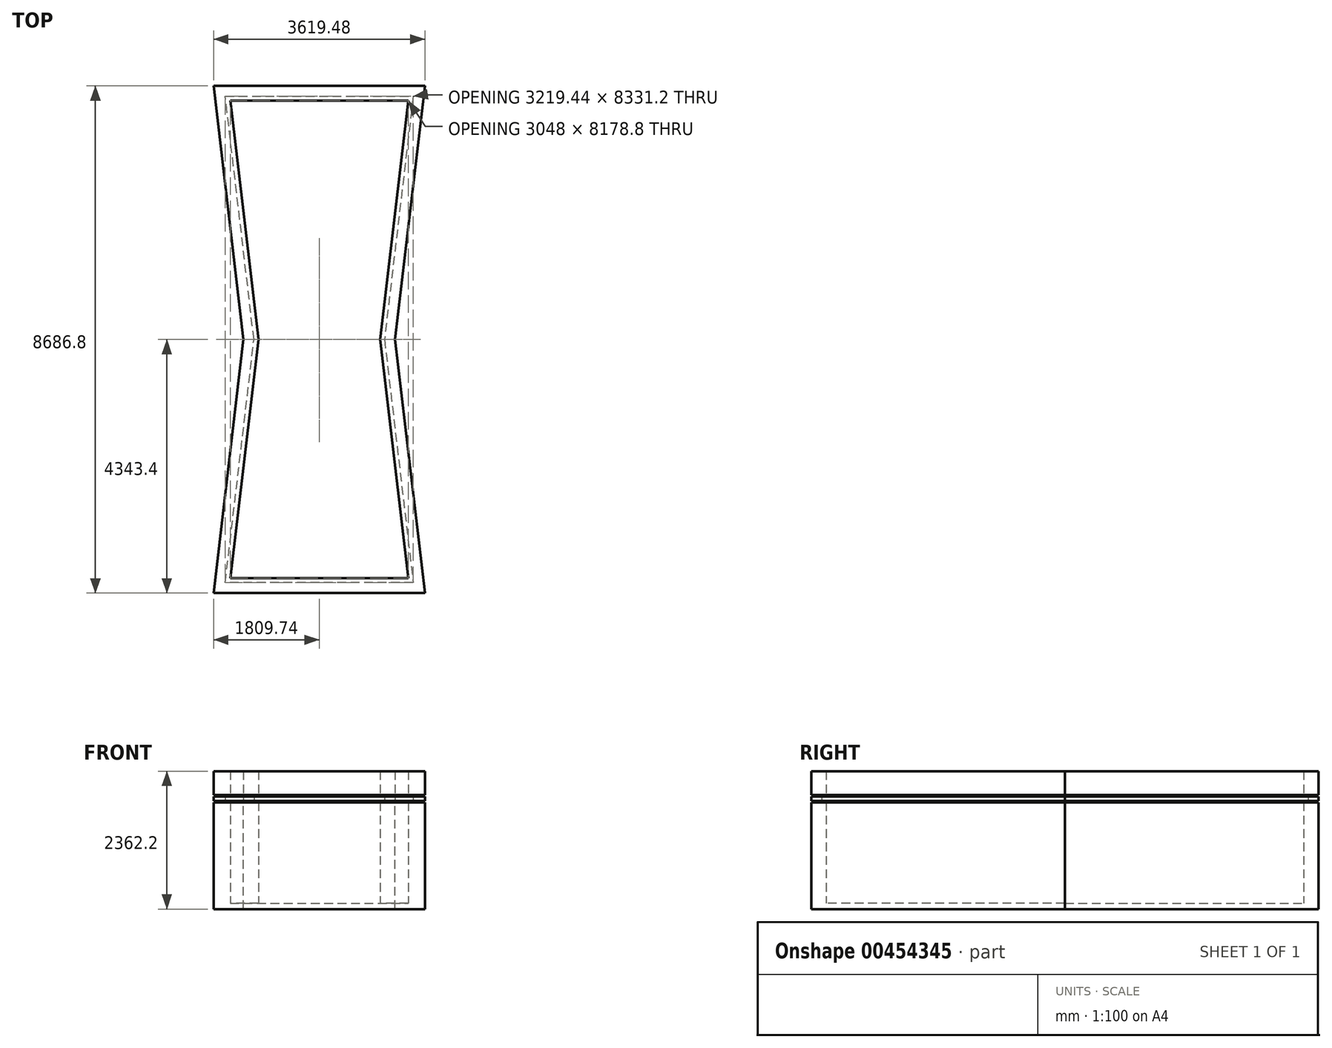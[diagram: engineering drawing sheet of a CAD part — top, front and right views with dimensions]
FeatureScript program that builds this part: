
annotation { "Feature Type Name" : "Feature", "Feature Type Description" : "" }
export const myFeature = defineFeature(function(context is Context, id is Id, definition is map)
    precondition{}
    {
        {
            var Q0;
            Q0=qCreatedBy(makeId("Top.planeOp"),FACE);
            var sketch = newSketch(context, id + "F0", { "sketchPlane" : qUnion([Q0])});
            skLineSegment(sketch, "E0", {"start": v(-1809.74, -4343.4) * mm, "end": v(-1297.16, 0) * mm});
            skLineSegment(sketch, "E1", {"start": v(-1297.16, 0) * mm, "end": v(-1809.74, 4343.4) * mm});
            skLineSegment(sketch, "E2", {"start": v(-1809.74, 4343.4) * mm, "end": v(1809.74, 4343.4) * mm});
            skLineSegment(sketch, "E3", {"start": v(1809.74, 4343.4) * mm, "end": v(1297.16, 0) * mm});
            skLineSegment(sketch, "E4", {"start": v(1297.16, 0) * mm, "end": v(1809.74, -4343.4) * mm});
            skLineSegment(sketch, "E5", {"start": v(1809.74, -4343.4) * mm, "end": v(-1809.74, -4343.4) * mm});
            skLineSegment(sketch, "E6", {"start": v(-1524, 4089.4) * mm, "end": v(1524, 4089.4) * mm});
            skLineSegment(sketch, "E7", {"start": v(1524, 4089.4) * mm, "end": v(1041.4, 0) * mm});
            skLineSegment(sketch, "E8", {"start": v(1041.4, 0) * mm, "end": v(1524, -4089.4) * mm});
            skLineSegment(sketch, "E9", {"start": v(1524, -4089.4) * mm, "end": v(-1524, -4089.4) * mm});
            skLineSegment(sketch, "E10", {"start": v(-1524, -4089.4) * mm, "end": v(-1041.4, 0) * mm});
            skLineSegment(sketch, "E11", {"start": v(-1041.4, 0) * mm, "end": v(-1524, 4089.4) * mm});
            skSolve(sketch);
        }
        {
            var Q0;
            Q0=makeQuery(id+"F0.imprint","IMPRINT",FACE,{"disambiguationData":[TD([[makeQuery(id+"F0.imprint","IMPRINT",EDGE,{"derivedFrom":sQuery(id+"F0.wireOp",EDGE,"E6")}),-1.0]])]});
            var Q1;
            Q1=makeQuery(id+"F0.imprint","IMPRINT",FACE,{"disambiguationData":[TD([[makeQuery(id+"F0.imprint","IMPRINT",EDGE,{"derivedFrom":sQuery(id+"F0.wireOp",EDGE,"E0")}),-1.0]])]});
            extrude(context, id + "F1", {"entities" : qUnion([Q0, Q1]), "oppositeDirection" : true, "depth" : 101.6 * mm});
        }
        {
            var Q0;
            Q0 = qSketchRegion(id + "F0", true);
            extrude(context, id + "F2", {"entities" : qUnion([Q0]), "operationType" : NewBodyOperationType.ADD, "depth" : 1727.2 * mm});
        }
        {
            var Q0;
            Q0=makeQuery(id+"F2.opExtrude","CAP_FACE",FACE,{"disambiguationData":[OSD([sQuery(id+"F0.wireOp",EDGE,"E0"),sQuery(id+"F0.wireOp",EDGE,"E1"),sQuery(id+"F0.wireOp",EDGE,"E2"),sQuery(id+"F0.wireOp",EDGE,"E3"),sQuery(id+"F0.wireOp",EDGE,"E4"),sQuery(id+"F0.wireOp",EDGE,"E5"),sQuery(id+"F0.wireOp",EDGE,"E6"),sQuery(id+"F0.wireOp",EDGE,"E7"),sQuery(id+"F0.wireOp",EDGE,"E8"),sQuery(id+"F0.wireOp",EDGE,"E9"),sQuery(id+"F0.wireOp",EDGE,"E10"),sQuery(id+"F0.wireOp",EDGE,"E11")])],"isStart":false});
            cPlane(context, id + "F3", {"entities" : qUnion([Q0]), "cplaneType" : CPlaneType.OFFSET, "offset" : 25.4 * mm, "width" : 152.4 * mm, "height" : 152.4 * mm});
        }
        {
            var Q0;
            Q0=qCreatedBy(id+"F3.planeOp",FACE);
            var sketch = newSketch(context, id + "F4", { "sketchPlane" : qUnion([Q0])});
            skLineSegment(sketch, "E12", {"start": v(-1809.74, -4343.4) * mm, "end": v(-1297.16, 0) * mm});
            skLineSegment(sketch, "E13", {"start": v(-1297.16, 0) * mm, "end": v(-1809.74, 4343.4) * mm});
            skLineSegment(sketch, "E14", {"start": v(-1809.74, 4343.4) * mm, "end": v(1809.74, 4343.4) * mm});
            skLineSegment(sketch, "E15", {"start": v(1809.74, 4343.4) * mm, "end": v(1297.16, 0) * mm});
            skLineSegment(sketch, "E16", {"start": v(1297.16, 0) * mm, "end": v(1809.74, -4343.4) * mm});
            skLineSegment(sketch, "E17", {"start": v(1809.74, -4343.4) * mm, "end": v(-1809.74, -4343.4) * mm});
            skLineSegment(sketch, "E18", {"start": v(-1609.72, -4165.6) * mm, "end": v(-1118.13, 0) * mm});
            skLineSegment(sketch, "E19", {"start": v(-1118.13, 0) * mm, "end": v(-1609.72, 4165.6) * mm});
            skLineSegment(sketch, "E20", {"start": v(-1609.72, 4165.6) * mm, "end": v(1609.72, 4165.6) * mm});
            skLineSegment(sketch, "E21", {"start": v(1609.72, 4165.6) * mm, "end": v(1118.13, 0) * mm});
            skLineSegment(sketch, "E22", {"start": v(1118.13, 0) * mm, "end": v(1609.72, -4165.6) * mm});
            skLineSegment(sketch, "E23", {"start": v(1609.72, -4165.6) * mm, "end": v(-1609.72, -4165.6) * mm});
            skLineSegment(sketch, "E24", {"start": v(-1524, 4089.4) * mm, "end": v(1524, 4089.4) * mm});
            skLineSegment(sketch, "E25", {"start": v(1524, 4089.4) * mm, "end": v(1041.4, 0) * mm});
            skLineSegment(sketch, "E26", {"start": v(1041.4, 0) * mm, "end": v(1524, -4089.4) * mm});
            skLineSegment(sketch, "E27", {"start": v(1524, -4089.4) * mm, "end": v(-1524, -4089.4) * mm});
            skLineSegment(sketch, "E28", {"start": v(-1524, -4089.4) * mm, "end": v(-1041.4, 0) * mm});
            skLineSegment(sketch, "E29", {"start": v(-1041.4, 0) * mm, "end": v(-1524, 4089.4) * mm});
            skSolve(sketch);
        }
        {
            var Q0;
            Q0 = qSketchRegion(id + "F4", true);
            extrude(context, id + "F5", {"entities" : qUnion([Q0]), "depth" : 76.2 * mm});
        }
        {
            var Q0;
            Q0=makeQuery(id+"F5.opExtrude","CAP_FACE",FACE,{"disambiguationData":[OSD([sQuery(id+"F4.wireOp",EDGE,"E12"),sQuery(id+"F4.wireOp",EDGE,"E13"),sQuery(id+"F4.wireOp",EDGE,"E14"),sQuery(id+"F4.wireOp",EDGE,"E15"),sQuery(id+"F4.wireOp",EDGE,"E16"),sQuery(id+"F4.wireOp",EDGE,"E17"),sQuery(id+"F4.wireOp",EDGE,"E18"),sQuery(id+"F4.wireOp",EDGE,"E19"),sQuery(id+"F4.wireOp",EDGE,"E20"),sQuery(id+"F4.wireOp",EDGE,"E21"),sQuery(id+"F4.wireOp",EDGE,"E22"),sQuery(id+"F4.wireOp",EDGE,"E23")])],"isStart":false});
            cPlane(context, id + "F6", {"entities" : qUnion([Q0]), "cplaneType" : CPlaneType.OFFSET, "offset" : 25.4 * mm, "width" : 152.4 * mm, "height" : 152.4 * mm});
        }
        {
            var Q0;
            Q0=qCreatedBy(id+"F6.planeOp",FACE);
            var sketch = newSketch(context, id + "F7", { "sketchPlane" : qUnion([Q0])});
            skLineSegment(sketch, "E30", {"start": v(-1809.74, -4343.4) * mm, "end": v(-1297.16, 0) * mm});
            skLineSegment(sketch, "E31", {"start": v(-1297.16, 0) * mm, "end": v(-1809.74, 4343.4) * mm});
            skLineSegment(sketch, "E32", {"start": v(-1809.74, 4343.4) * mm, "end": v(1809.74, 4343.4) * mm});
            skLineSegment(sketch, "E33", {"start": v(1809.74, 4343.4) * mm, "end": v(1297.16, 0) * mm});
            skLineSegment(sketch, "E34", {"start": v(1297.16, 0) * mm, "end": v(1809.74, -4343.4) * mm});
            skLineSegment(sketch, "E35", {"start": v(1809.74, -4343.4) * mm, "end": v(-1809.74, -4343.4) * mm});
            skLineSegment(sketch, "E36", {"start": v(-1524, 4089.4) * mm, "end": v(1524, 4089.4) * mm});
            skLineSegment(sketch, "E37", {"start": v(1524, 4089.4) * mm, "end": v(1041.4, 0) * mm});
            skLineSegment(sketch, "E38", {"start": v(1041.4, 0) * mm, "end": v(1524, -4089.4) * mm});
            skLineSegment(sketch, "E39", {"start": v(1524, -4089.4) * mm, "end": v(-1524, -4089.4) * mm});
            skLineSegment(sketch, "E40", {"start": v(-1524, -4089.4) * mm, "end": v(-1041.4, 0) * mm});
            skLineSegment(sketch, "E41", {"start": v(-1041.4, 0) * mm, "end": v(-1524, 4089.4) * mm});
            skSolve(sketch);
        }
        {
            var Q0;
            Q0 = qSketchRegion(id + "F7", true);
            extrude(context, id + "F8", {"entities" : qUnion([Q0]), "depth" : 406.4 * mm});
        }
    });
